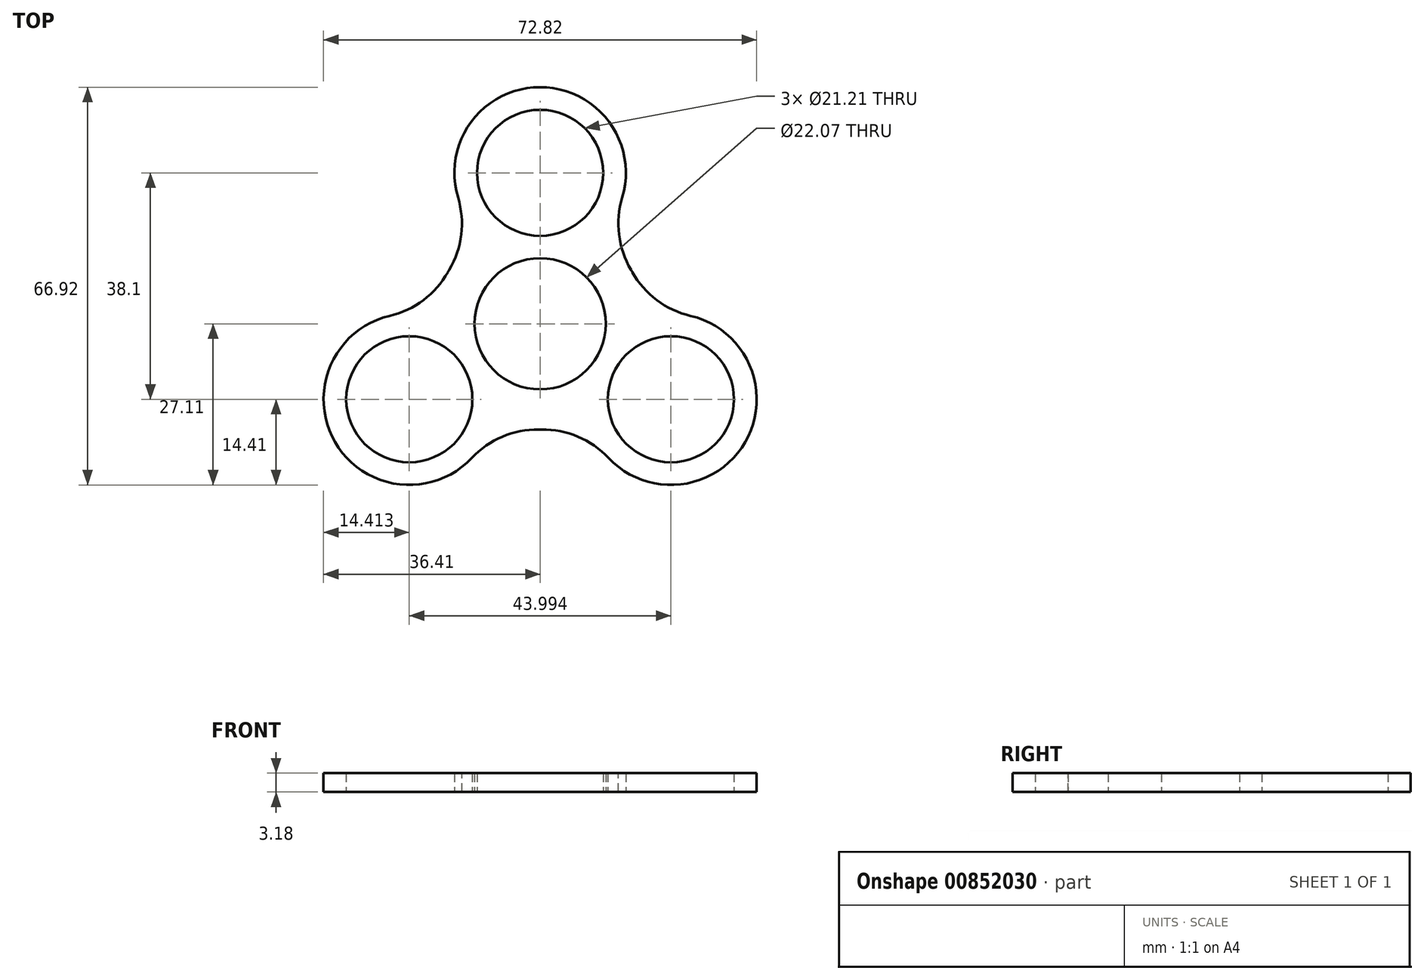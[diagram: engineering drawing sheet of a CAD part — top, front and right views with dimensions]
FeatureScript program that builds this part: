
annotation { "Feature Type Name" : "Feature", "Feature Type Description" : "" }
export const myFeature = defineFeature(function(context is Context, id is Id, definition is map)
    precondition{}
    {
        {
            var Q0;
            Q0=qCreatedBy(makeId("Top.planeOp"),FACE);
            var sketch = newSketch(context, id + "F0", { "sketchPlane" : qUnion([Q0])});
            skLineSegment(sketch, "E0", {"start": v(0, 0) * mm, "end": v(0, 25.4) * mm});
            skCircle(sketch, "E1", {"center": v(0, 25.4) * mm, "radius": 10.6 * mm});
            skCircle(sketch, "E2", {"center": v(0, 0) * mm, "radius": 11.04 * mm});
            skCircle(sketch, "E3", {"center": v(0, 25.4) * mm, "radius": 14.41 * mm});
            skCircle(sketch, "E4.1.0", {"center": v(-22, -12.7) * mm, "radius": 14.41 * mm});
            skCircle(sketch, "E4.1.1", {"center": v(-22, -12.7) * mm, "radius": 10.6 * mm});
            skCircle(sketch, "E4.2.0", {"center": v(22, -12.7) * mm, "radius": 14.41 * mm});
            skCircle(sketch, "E4.2.1", {"center": v(22, -12.7) * mm, "radius": 10.6 * mm});
            skCircle(sketch, "E5", {"center": v(0, 0) * mm, "radius": 17.78 * mm});
            skSolve(sketch);
        }
        {
            var Q0;
            Q0=qSketchRegion(id+"F0",true);
            extrude(context, id + "F1", {"entities" : qUnion([Q0]), "depth" : 3.17 * mm, "offsetDistance" : 25.4 * mm});
        }
        {
            var Q0;
            {var subQ0=sQuery(id+"F0.wireOp",EDGE,"E5");var subQ1=sQuery(id+"F0.wireOp",EDGE,"E3");Q0=makeQuery(id+"F1.opExtrude","SWEPT_EDGE",EDGE,{"disambiguationData":[OSD([subQ1,subQ0]),TDD([makeQuery(id+"F0.imprint","INTERSECT",VERTEX,{"disambiguationData":[OD(0.0)],"derivedFrom":[subQ1,subQ0]})])]});}
            var Q1;
            {var subQ0=sQuery(id+"F0.wireOp",EDGE,"E5");var subQ1=sQuery(id+"F0.wireOp",EDGE,"E4.1.0");Q1=makeQuery(id+"F1.opExtrude","SWEPT_EDGE",EDGE,{"disambiguationData":[OSD([subQ1,subQ0]),TDD([makeQuery(id+"F0.imprint","INTERSECT",VERTEX,{"disambiguationData":[OD(0.0)],"derivedFrom":[subQ1,subQ0]})])]});}
            var Q2;
            {var subQ0=sQuery(id+"F0.wireOp",EDGE,"E5");var subQ1=sQuery(id+"F0.wireOp",EDGE,"E4.1.0");Q2=makeQuery(id+"F1.opExtrude","SWEPT_EDGE",EDGE,{"disambiguationData":[OSD([subQ1,subQ0]),TDD([makeQuery(id+"F0.imprint","INTERSECT",VERTEX,{"disambiguationData":[OD(1.0)],"derivedFrom":[subQ1,subQ0]})])]});}
            var Q3;
            {var subQ0=sQuery(id+"F0.wireOp",EDGE,"E5");var subQ1=sQuery(id+"F0.wireOp",EDGE,"E4.2.0");Q3=makeQuery(id+"F1.opExtrude","SWEPT_EDGE",EDGE,{"disambiguationData":[OSD([subQ1,subQ0]),TDD([makeQuery(id+"F0.imprint","INTERSECT",VERTEX,{"disambiguationData":[OD(0.0)],"derivedFrom":[subQ1,subQ0]})])]});}
            var Q4;
            {var subQ0=sQuery(id+"F0.wireOp",EDGE,"E5");var subQ1=sQuery(id+"F0.wireOp",EDGE,"E4.2.0");Q4=makeQuery(id+"F1.opExtrude","SWEPT_EDGE",EDGE,{"disambiguationData":[OSD([subQ1,subQ0]),TDD([makeQuery(id+"F0.imprint","INTERSECT",VERTEX,{"disambiguationData":[OD(1.0)],"derivedFrom":[subQ1,subQ0]})])]});}
            var Q5;
            {var subQ0=sQuery(id+"F0.wireOp",EDGE,"E5");var subQ1=sQuery(id+"F0.wireOp",EDGE,"E3");Q5=makeQuery(id+"F1.opExtrude","SWEPT_EDGE",EDGE,{"disambiguationData":[OSD([subQ1,subQ0]),TDD([makeQuery(id+"F0.imprint","INTERSECT",VERTEX,{"disambiguationData":[OD(1.0)],"derivedFrom":[subQ1,subQ0]})])]});}
            fillet(context, id + "F2", {"entities" : qUnion([Q0, Q1, Q2, Q3, Q4, Q5]), "radius" : 15.24 * mm, "tangentPropagation" : true, "allowEdgeOverflow" : false});
        }
    });
